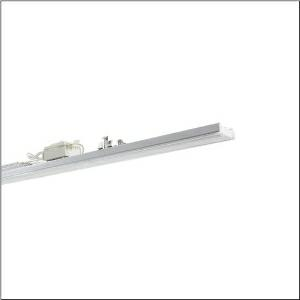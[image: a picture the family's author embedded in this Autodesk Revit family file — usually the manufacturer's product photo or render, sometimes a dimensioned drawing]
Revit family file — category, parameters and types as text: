
# Revit family: licross_21_recessed_mo_52tl18cn49xg
name_source: partatom
category: Lighting Fixtures
units: mm (PartAtom-declared; Revit-internal decimal feet)

## family parameters
Cut with Voids When Loaded = No
Host = Face
Light Source = No
Part Type = Normal
Room Calculation Point = No
Round Connector Dimension = Use Diameter
Shared = No

## types (1)
- --- (1 x LED, 9000 lm, 49.9 W, 4000K)
    Apparent Load = 50 VA
    CIE Flux Codes = 79 95 99 100 100
    Color Rendering = 80
    Color Temperature = 4000K
    Default Elevation = 1800 mm
    Description = Licross 21 Recessed MO, luminaire insert, of sheet steel, galvanised, coil coated, white, length: 1.500mm, width: 66mm, height: 67mm, LED rated luminous flux: 9.000lm, light colour: 840, SDCM (Standard Deviation of Colour Matching)MacAdam ≤ 3 SDCM (initial), control gear: ON/OFF Multilumen, CLOi, with plug, 3-pole, with phase selection, mains connection: 220..240V, AC, 50/60Hz, internal wiring halogen-free, primary light control with lens, of plastic, primary optical cover: cover, of PMMA, light emission: direct distribution, primary light characteristic: symmetric, protection rating (complete): IP40, insulation class (complete): insulation class I (protective earthing), certification: CE, ENEC, VDE, UKCA, protection symbol: D if used in an environment without relevant dust loads with corresponding accessories, impact resistance: IK06, permissible ambient temperature for indoor applications: -35..+40°C, corresponds to IFS (International Featured Standards) requirements for safety and quality in the food industry, reducing of maximum allowable ambient temperature of 5°C with ceiling mounting, LABS conformity tested according to VDMA 24364:2018-05, The light source and the operating device comply with the requirements of the Ecodesign Regulation (EU) 2019/2020 and are replaceable in accordance with this regulation, packaging unit: 1 piece
    Height = 58 mm
    Lamp = 1 x LED
    Lamp Light Flux = 9000 lm
    Lamp Power = 49.9 W
    Lamp count = 1
    Length = 1500 mm
    Luminous efficacy = 180 lm/W
    Manufacturer = Siteco
    ModVariant = No
    Model = 52TL18CN49XG
    Mounting Place = Ceiling
    Mounting Type = Pendant
    Number of Poles = 1
    OnlyDefault = Yes
    Power Factor = 1
    Product Name = Licross 21 Recessed MO
    Product group = luminaire insert | ceiling pendant
    ProductGroupID = 901
    Protection Class = Protection class I
    Protection Degree = IP 40
    RLX_Detail_Level = 1
    RLX_Emergency_Light_Flux = 0 lm
    RLX_Emergency_Type = 0
    RLX_Emergency_Type_DB = No
    RlxData = <blob elided: 22557 chars, md5=1a61e7eb>
    Socket = socket
    Standby Power = 0 W
    System Light Flux = 9000 lm
    System Power = 50 W
    Type Comments = factory setting: luminous flux: 100 % | (A | C | E) | 116 mA
    Type Image = l_1296930.jpg
    URL = http://relux.com
    VarID = @adj_109981
    Voltage = 0 V
    Weight = 0.00 kg
    Width = 66 mm

## geometry (parser evidence)
native form markers: Blend x4, Sweep x9
no freeform markers — native parametric forms only
